# Revit family: Sink_Kitchen-Fire_Clay-DXV-Orchard-D20101000_Series
name_source: partatom
category: Plumbing Fixtures
revit_build: Autodesk Revit 2014 (Build: 20130308_1515(x64)
units: mm (PartAtom-declared; Revit-internal decimal feet)

## types (3) — shared parameters
Assembly Code = D2010310
Basin Shape = Rectangle
CW Connection = Yes
CWFU = 1.5
Cold Water Connection Diameter = 1/2"
Cold Water Connection Height = 22 3/4"
Cold Water Connection Radius = 1/4"
Cold Water Connection Width = 4"
Default Elevation = 34"
HW Connection = Yes
HWFU = 1.5
Height = 10"
Hot Water Connection Diameter = 1/2"
Hot Water Connection Height = 22 3/4"
Hot Water Connection Radius = 1/4"
Hot Water Connection Width = 4"
Installation Type = Semi Counter Mounted
Length = 18"
Manufacturer = DXV
Price = Prices may vary. Please consult Manufacturer Representative for most up-to-date price list.
Product Documentation Link = http://dxv.blob.core.windows.net
Product Page URL = http://www.dxv.com
Type Comments = Bottom sink rack and strainer included
URL = www.dxv.com
Vent Connection = No
WFU = 2
Waste Connection = Yes
Waste Connection Diameter = 1 1/4"
Waste Connection Height = 20 1/4"
Waste Connection Radius = 5/8"
Width = 24"

## per-type parameters (varying)
| type | Description | Finish | Material |
| D20101000.415 | Apron Front Kitchen Sink Canvas White | Fire Clay-DXV-415-Canvas White | Fire Clay-DXV-415-Canvas White |
| D20101000.425 | Apron Front Kitchen Sink Chenille Gray | Fire Clay-DXV-425-Chenille Gray | Fire Clay-DXV-425-Chenille Gray |
| D20101000.410 | Apron Front Kitchen Sink Oyster | Fire Clay-DXV-410-Oyster | Fire Clay-DXV-410-Oyster |

note: column(s) folded — value = type name in every type: Model

## geometry (parser evidence)
native form markers: Sweep x1
no freeform markers — native parametric forms only
